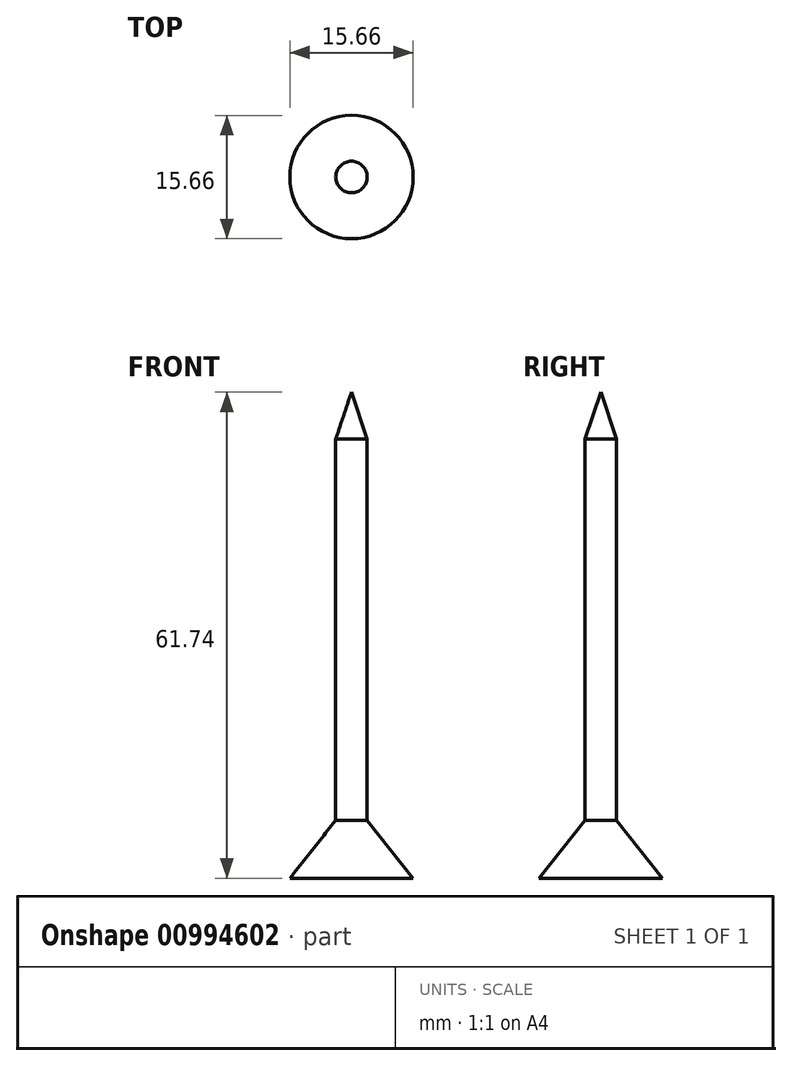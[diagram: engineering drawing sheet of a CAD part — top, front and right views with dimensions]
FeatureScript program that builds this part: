
annotation { "Feature Type Name" : "Feature", "Feature Type Description" : "" }
export const myFeature = defineFeature(function(context is Context, id is Id, definition is map)
    precondition{}
    {
        {
            var Q0;
            Q0=qCreatedBy(makeId("Front.planeOp"),FACE);
            var sketch = newSketch(context, id + "F0", { "sketchPlane" : qUnion([Q0])});
            skLineSegment(sketch, "E0", {"start": v(-30, 0) * mm, "end": v(30.83, 0) * mm});
            skLineSegment(sketch, "E1", {"start": v(30.83, 0) * mm, "end": v(30.83, 15.17) * mm});
            skLineSegment(sketch, "E2", {"start": v(7.83, 0) * mm, "end": v(2, 7.33) * mm});
            skLineSegment(sketch, "E3", {"start": v(2, 7.33) * mm, "end": v(0, 7.33) * mm});
            skLineSegment(sketch, "E4", {"start": v(0, 7.33) * mm, "end": v(0, 61.74) * mm});
            skLineSegment(sketch, "E5", {"start": v(0, 61.74) * mm, "end": v(2, 55.8) * mm});
            skLineSegment(sketch, "E6", {"start": v(2, 55.8) * mm, "end": v(2, 7.33) * mm});
            skLineSegment(sketch, "E7", {"start": v(0, 7.33) * mm, "end": v(0, 0) * mm});
            skSolve(sketch);
        }
        {
            var Q0;
            {var subQ0=sQuery(id+"F0.wireOp",EDGE,"E2");Q0=makeQuery(id+"F0.imprint","IMPRINT",FACE,{"disambiguationData":[TD([[makeQuery(id+"F0.imprint","IMPRINT",EDGE,{"derivedFrom":subQ0}),1.0]])]});}
            var Q1;
            Q1=makeQuery(id+"F0.imprint","IMPRINT",FACE,{"disambiguationData":[TD([[makeQuery(id+"F0.imprint","IMPRINT",EDGE,{"derivedFrom":sQuery(id+"F0.wireOp",EDGE,"E3")}),-1.0]])]});
            var Q2;
            Q2=sQuery(id+"F0.wireOp",EDGE,"E4");
            revolve(context, id + "F1", {"surfaceOperationType" : NewSurfaceOperationType.NEW, "entities" : qUnion([Q0, Q1]), "axis" : qUnion([Q2]), "revolveType" : RevolveType.FULL});
        }
    });
